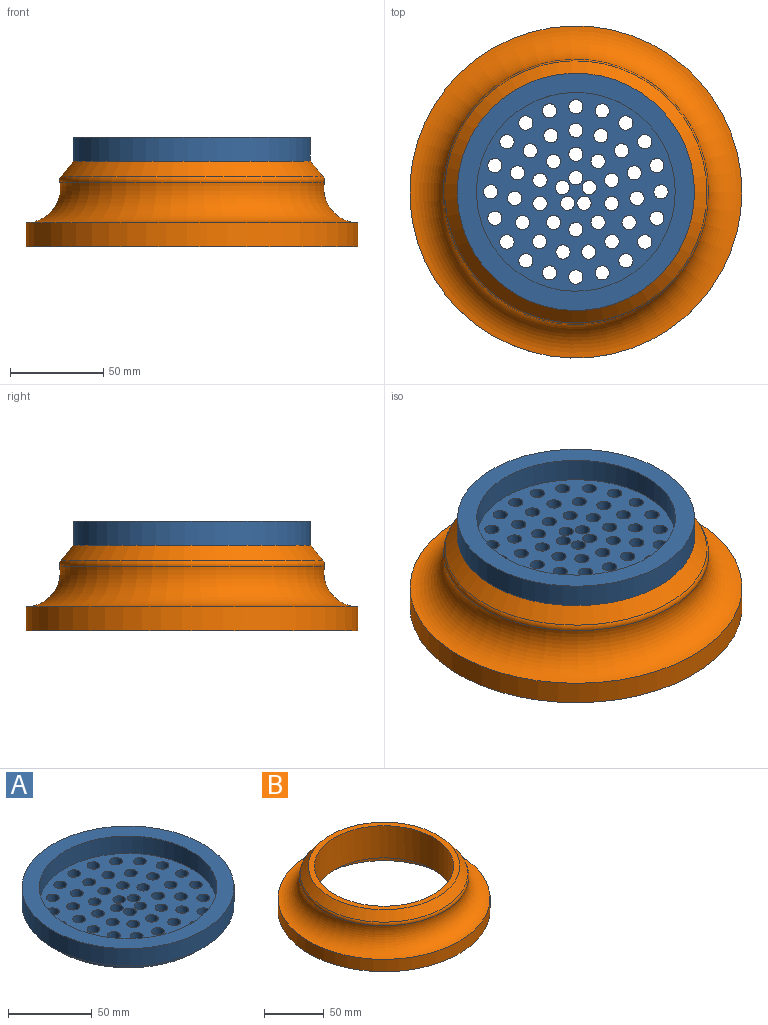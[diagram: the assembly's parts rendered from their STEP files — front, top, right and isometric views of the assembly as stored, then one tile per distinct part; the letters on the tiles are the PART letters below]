
ASSEMBLY  parts=2 mates=1
PART A: 57 faces, bbox 127x127x17.8 mm
  f0: cylinder r=63.5mm len=127mm, axis (0,0,-1), area 5067.1mm2, adj f2,f3
  f1: cylinder r=53.21mm len=106.43mm, axis (0,0,-1), area 4246.2mm2, adj f2,f4
  f2: plane 127x127mm, normal (0,0,1), area 3771.9mm2, adj f0,f1
  f3: plane 127x127mm, normal (0,0,-1), area 1992.3mm2, adj f0,f54
  f4: plane 106.43x106.43mm, normal (0,0,1), area 6615.6mm2, adj f1,f5,f6,f7,f8,f9,f10,f11
  f5: cylinder r=3.81mm len=7.62mm, axis (0,0,1), area 121.6mm2, adj f4,f56
  f6: cylinder r=3.81mm len=7.62mm, axis (0,0,1), area 121.6mm2, adj f4,f56
  f7: cylinder r=3.81mm len=7.62mm, axis (0,0,1), area 121.6mm2, adj f4,f56
  f8: cylinder r=3.81mm len=7.62mm, axis (0,0,1), area 121.6mm2, adj f4,f56
  f9: cylinder r=3.81mm len=7.62mm, axis (0,0,1), area 121.6mm2, adj f4,f56
  f10: cylinder r=3.81mm len=7.62mm, axis (0,0,1), area 121.6mm2, adj f4,f56
  f11: cylinder r=3.81mm len=7.62mm, axis (0,0,1), area 121.6mm2, adj f4,f56
  f12: cylinder r=3.81mm len=7.62mm, axis (0,0,1), area 121.6mm2, adj f4,f56
  f13: cylinder r=3.81mm len=7.62mm, axis (0,0,1), area 121.6mm2, adj f4,f56
  f14: cylinder r=3.81mm len=7.62mm, axis (0,0,1), area 121.6mm2, adj f4,f56
  f15: cylinder r=3.81mm len=7.62mm, axis (0,0,1), area 121.6mm2, adj f4,f56
  f16: cylinder r=3.81mm len=7.62mm, axis (0,0,1), area 121.6mm2, adj f4,f56
  f17: cylinder r=3.81mm len=7.62mm, axis (0,0,1), area 121.6mm2, adj f4,f56
  f18: cylinder r=3.81mm len=7.62mm, axis (0,0,1), area 121.6mm2, adj f4,f56
  f19: cylinder r=3.81mm len=7.62mm, axis (0,0,1), area 121.6mm2, adj f4,f56
  f20: cylinder r=3.81mm len=7.62mm, axis (0,0,1), area 121.6mm2, adj f4,f56
  f21: cylinder r=3.81mm len=7.62mm, axis (0,0,1), area 121.6mm2, adj f4,f56
  f22: cylinder r=3.81mm len=7.62mm, axis (0,0,1), area 121.6mm2, adj f4,f56
  f23: cylinder r=3.81mm len=7.62mm, axis (0,0,1), area 121.6mm2, adj f4,f56
  f24: cylinder r=3.81mm len=7.62mm, axis (0,0,1), area 121.6mm2, adj f4,f56
  f25: cylinder r=3.81mm len=7.62mm, axis (0,0,1), area 121.6mm2, adj f4,f56
  f26: cylinder r=3.81mm len=7.62mm, axis (0,0,1), area 121.6mm2, adj f4,f56
  f27: cylinder r=3.81mm len=7.62mm, axis (0,0,1), area 121.6mm2, adj f4,f56
  f28: cylinder r=3.81mm len=7.62mm, axis (0,0,1), area 121.6mm2, adj f4,f56
  f29: cylinder r=3.81mm len=7.62mm, axis (0,0,1), area 121.6mm2, adj f4,f56
  f30: cylinder r=3.81mm len=7.62mm, axis (0,0,1), area 121.6mm2, adj f4,f56
  f31: cylinder r=3.81mm len=7.62mm, axis (0,0,1), area 121.6mm2, adj f4,f56
  f32: cylinder r=3.81mm len=7.62mm, axis (0,0,1), area 121.6mm2, adj f4,f56
  f33: cylinder r=3.81mm len=7.62mm, axis (0,0,1), area 121.6mm2, adj f4,f56
  f34: cylinder r=3.81mm len=7.62mm, axis (0,0,1), area 121.6mm2, adj f4,f56
  f35: cylinder r=3.81mm len=7.62mm, axis (0,0,1), area 121.6mm2, adj f4,f56
  f36: cylinder r=3.81mm len=7.62mm, axis (0,0,1), area 121.6mm2, adj f4,f56
  f37: cylinder r=3.81mm len=7.62mm, axis (0,0,1), area 121.6mm2, adj f4,f56
  f38: cylinder r=3.81mm len=7.62mm, axis (0,0,1), area 121.6mm2, adj f4,f56
  f39: cylinder r=3.81mm len=7.62mm, axis (0,0,1), area 121.6mm2, adj f4,f56
  f40: cylinder r=3.81mm len=7.62mm, axis (0,0,1), area 121.6mm2, adj f4,f56
  f41: cylinder r=3.81mm len=7.62mm, axis (0,0,1), area 121.6mm2, adj f4,f56
  f42: cylinder r=3.81mm len=7.62mm, axis (0,0,1), area 121.6mm2, adj f4,f56
  f43: cylinder r=3.81mm len=7.62mm, axis (0,0,1), area 121.6mm2, adj f4,f56
  f44: cylinder r=3.81mm len=7.62mm, axis (0,0,1), area 121.6mm2, adj f4,f56
  f45: cylinder r=3.81mm len=7.62mm, axis (0,0,1), area 121.6mm2, adj f4,f56
  f46: cylinder r=3.81mm len=7.62mm, axis (0,0,1), area 121.6mm2, adj f4,f56
  f47: cylinder r=3.81mm len=7.62mm, axis (0,0,1), area 121.6mm2, adj f4,f56
  f48: cylinder r=3.81mm len=7.62mm, axis (0,0,1), area 121.6mm2, adj f4,f56
  f49: cylinder r=3.81mm len=7.62mm, axis (0,0,1), area 121.6mm2, adj f4,f56
  f50: cylinder r=3.81mm len=7.62mm, axis (0,0,1), area 121.6mm2, adj f4,f56
  f51: cylinder r=3.81mm len=7.62mm, axis (0,0,1), area 121.6mm2, adj f4,f56
  f52: cylinder r=3.81mm len=7.62mm, axis (0,0,1), area 121.6mm2, adj f4,f56
  f53: cylinder r=3.81mm len=7.62mm, axis (0,0,1), area 121.6mm2, adj f4,f56
  f54: cylinder r=58.29mm len=116.59mm, axis (0,0,1), area 1860.6mm2, adj f3,f56
  f55: cylinder r=3.81mm len=7.62mm, axis (0,0,1), area 121.6mm2, adj f4,f56
  f56: plane 116.59x116.59mm, normal (0,0,-1), area 8395.2mm2, adj f5,f6,f7,f8,f9,f10,f11,f12
PART B: 9 faces, bbox 192.8x192.8x45.7 mm
  f0: cylinder r=58.42mm len=116.84mm, axis (0,0,1), area 12120.4mm2, adj f1,f7
  f1: plane 127x127mm, normal (0,0,1), area 1945.8mm2, adj f0,f2
  f2: cone r=63.5mm half-angle=39.2deg, axis (0,0,-1), area 4403mm2, adj f1,f5
  f3: cylinder r=88.9mm len=177.8mm, axis (0,0,1), area 7093.9mm2, adj f4,f6
  f4: torus R=89.04mm, axis (0,0,1), area 15483.9mm2, adj f3,f5
  f5: torus R=67.18mm, axis (0,0,1), area 1470.9mm2, adj f2,f4
  f6: plane 177.8x177.8mm, normal (0,0,-1), area 8365.7mm2, adj f3,f8
  f7: plane 144.78x144.78mm, normal (0,0,-1), area 5741mm2, adj f0,f8
  f8: cylinder r=72.39mm len=144.78mm, axis (0,0,-1), area 5776.5mm2, adj f6,f7
PLACE A t=(-71.89,-32.44,36.46)mm
PLACE B t=(-71.89,-32.44,-9.26)mm
MATE fastened A.f0 <-> B.f2  axis (0,0,-1) through (-71.89,-32.44,36.46)mm
